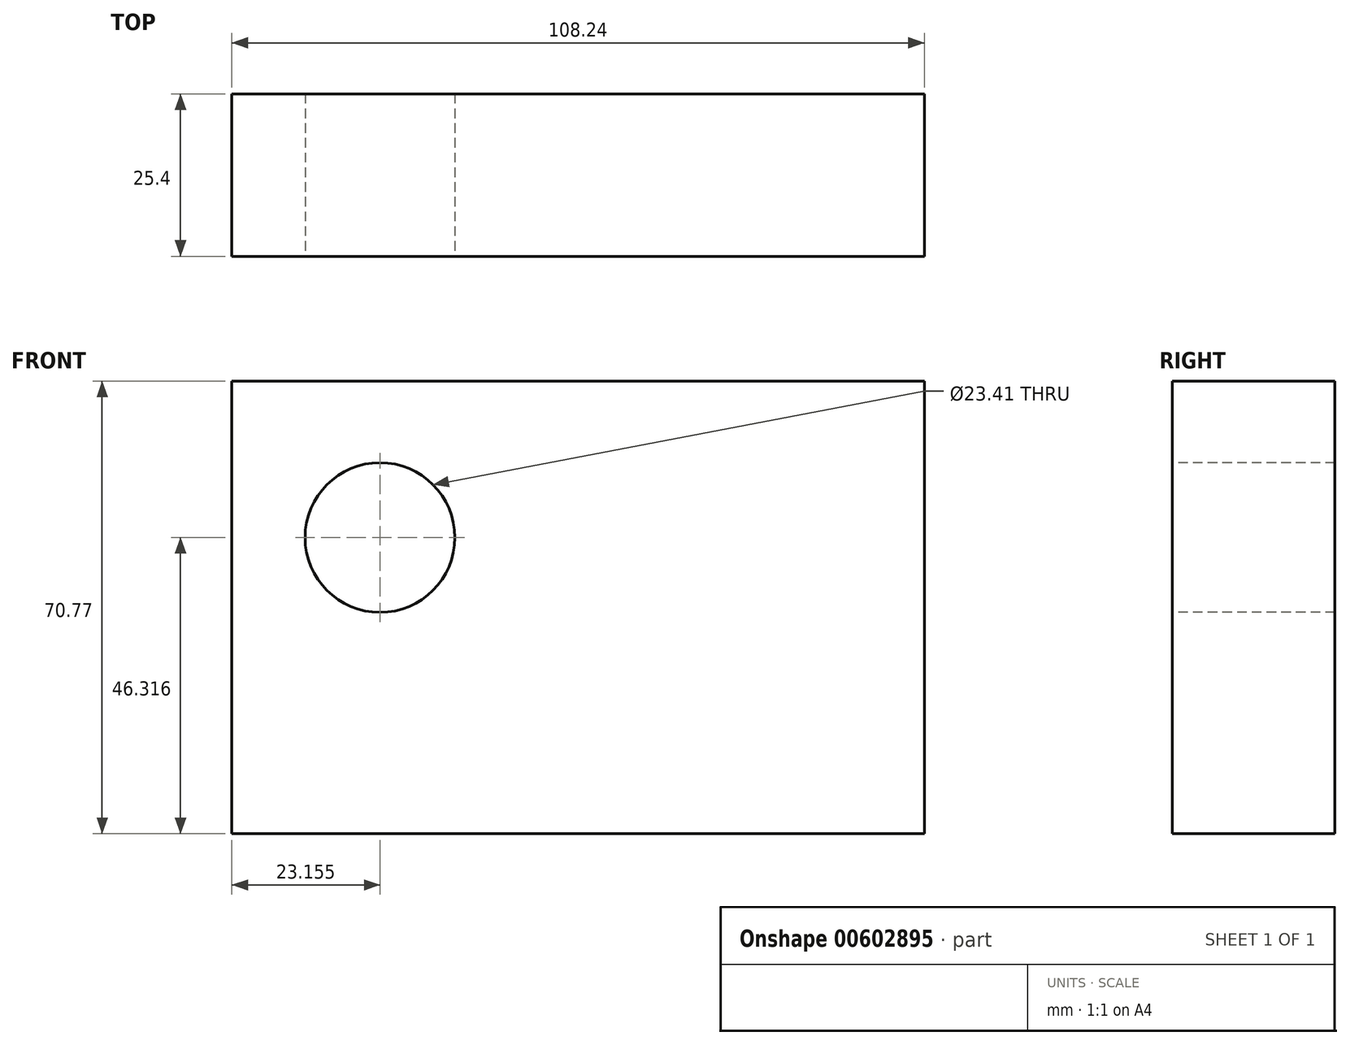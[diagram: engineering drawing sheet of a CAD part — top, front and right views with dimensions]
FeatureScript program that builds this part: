
annotation { "Feature Type Name" : "Feature", "Feature Type Description" : "" }
export const myFeature = defineFeature(function(context is Context, id is Id, definition is map)
    precondition{}
    {
        {
            var Q0;
            Q0=qCreatedBy(makeId("Front.planeOp"),FACE);
            var sketch = newSketch(context, id + "F0", { "sketchPlane" : qUnion([Q0])});
            skLineSegment(sketch, "E0.bottom", {"start": v(-49.37, -31.55) * mm, "end": v(58.87, -31.55) * mm});
            skLineSegment(sketch, "E0.top", {"start": v(-49.37, 39.22) * mm, "end": v(58.87, 39.22) * mm});
            skLineSegment(sketch, "E0.left", {"start": v(-49.37, -31.55) * mm, "end": v(-49.37, 39.22) * mm});
            skLineSegment(sketch, "E0.right", {"start": v(58.87, -31.55) * mm, "end": v(58.87, 39.22) * mm});
            skSolve(sketch);
        }
        {
            var Q0;
            Q0=makeQuery(id+"F0.imprint","IMPRINT",FACE,{"disambiguationData":[TD([[makeQuery(id+"F0.imprint","IMPRINT",EDGE,{"derivedFrom":sQuery(id+"F0.wireOp",EDGE,"E0.bottom")}),1.0]])]});
            extrude(context, id + "F1", {"entities" : qUnion([Q0]), "depth" : 25.4 * mm, "offsetDistance" : 25.4 * mm});
        }
        {
            var Q0;
            Q0=makeQuery(id+"F1.opExtrude","CAP_FACE",FACE,{"disambiguationData":[OSD([sQuery(id+"F0.wireOp",EDGE,"E0.bottom"),sQuery(id+"F0.wireOp",EDGE,"E0.top"),sQuery(id+"F0.wireOp",EDGE,"E0.left"),sQuery(id+"F0.wireOp",EDGE,"E0.right")])],"isStart":false});
            var sketch = newSketch(context, id + "F2", { "sketchPlane" : qUnion([Q0])});
            skCircle(sketch, "E1", {"center": v(-26.21, 14.77) * mm, "radius": 11.7 * mm});
            skSolve(sketch);
        }
        {
            var Q0;
            Q0 = qSketchRegion(id + "F2", true);
            extrude(context, id + "F3", {"entities" : qUnion([Q0]), "operationType" : NewBodyOperationType.REMOVE, "endBound" : BoundingType.THROUGH_ALL, "oppositeDirection" : true, "depth" : 25.4 * mm, "offsetDistance" : 25.4 * mm});
        }
    });
